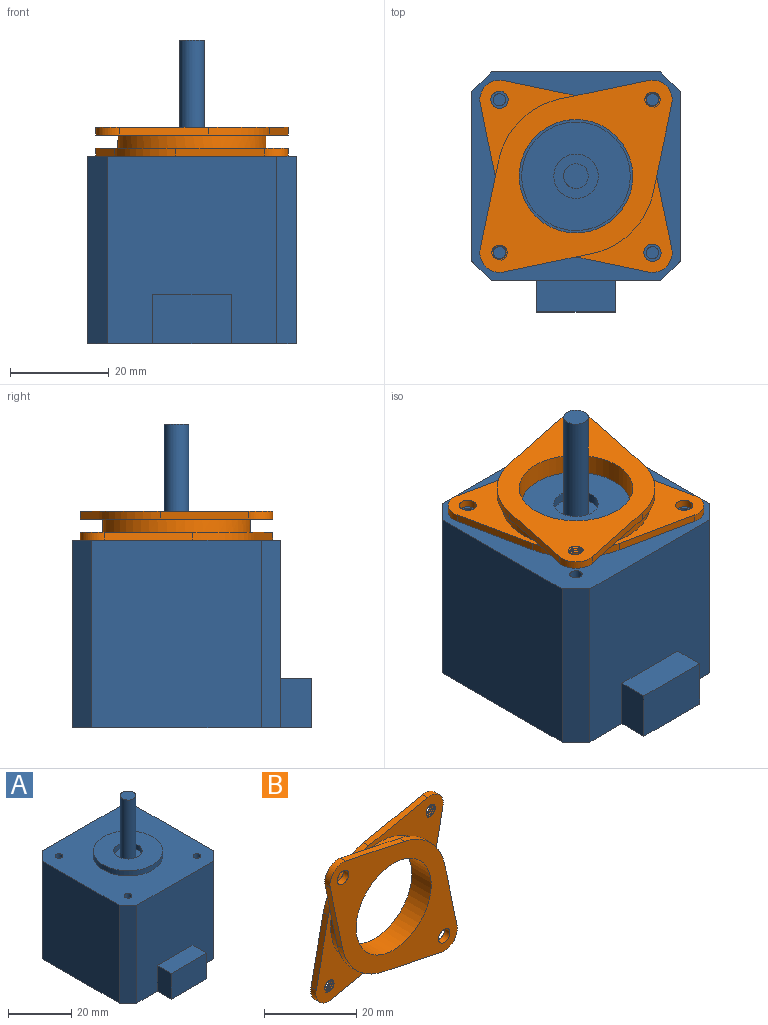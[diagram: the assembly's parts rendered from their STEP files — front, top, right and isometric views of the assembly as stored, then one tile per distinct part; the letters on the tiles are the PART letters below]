
ASSEMBLY  parts=2 mates=1
PART A: 28 faces, bbox 42.3x48.6x61.5 mm
  f0: plane 38x34.3mm, normal (0,-1,0), area 1143.4mm2, adj f4,f5,f20,f21,f22,f26,f27
  f1: plane 38x34.3mm, normal (1,0,0), area 1303.4mm2, adj f4,f5,f25,f26
  f2: plane 38x34.3mm, normal (0,1,0), area 1303.4mm2, adj f4,f5,f24,f25
  f3: plane 38x34.3mm, normal (-1,0,0), area 1303.4mm2, adj f4,f5,f24,f27
  f4: plane 48.6x42.3mm, normal (0,0,-1), area 1858.1mm2, adj f0,f1,f2,f3,f20,f22,f23,f24
  f5: plane 42.3x42.3mm, normal (0,0,1), area 1357.5mm2, adj f0,f1,f2,f3,f6,f8,f10,f12
  f6: cylinder r=1.25mm len=5mm, axis (0,0,1), area 39.3mm2, adj f5,f7
  f7: plane 2.5x2.5mm, normal (0,0,1), area 4.9mm2, adj f6
  f8: cylinder r=1.25mm len=5mm, axis (0,0,1), area 39.3mm2, adj f5,f9
  f9: plane 2.5x2.5mm, normal (0,0,1), area 4.9mm2, adj f8
  f10: cylinder r=1.25mm len=5mm, axis (0,0,1), area 39.3mm2, adj f5,f11
  f11: plane 2.5x2.5mm, normal (0,0,1), area 4.9mm2, adj f10
  f12: cylinder r=1.25mm len=5mm, axis (0,0,1), area 39.3mm2, adj f5,f13
  f13: plane 2.5x2.5mm, normal (0,0,1), area 4.9mm2, adj f12
  f14: cylinder r=4.5mm len=9mm, axis (0,0,-1), area 56.5mm2, adj f16,f17
  f15: cylinder r=11mm len=22mm, axis (0,0,-1), area 138.2mm2, adj f5,f16
  f16: plane 22x22mm, normal (0,0,1), area 316.5mm2, adj f14,f15
  f17: plane 9x9mm, normal (0,0,1), area 44mm2, adj f14,f19
  f18: plane 5x5mm, normal (0,0,1), area 19.6mm2, adj f19
  f19: cylinder r=2.5mm len=23.5mm, axis (0,0,-1), area 369.1mm2, adj f17,f18
  f20: plane 10x6.3mm, normal (1,0,0), area 63mm2, adj f0,f4,f21,f23
  f21: plane 16x6.3mm, normal (0,0,1), area 100.8mm2, adj f0,f20,f22,f23
  f22: plane 10x6.3mm, normal (-1,0,0), area 63mm2, adj f0,f4,f21,f23
  f23: plane 16x10mm, normal (0,-1,0), area 160mm2, adj f4,f20,f21,f22
  f24: plane 38x4mm, normal (-0.71,0.71,0), area 215mm2, adj f2,f3,f4,f5
  f25: plane 38x4mm, normal (0.71,0.71,0), area 215mm2, adj f1,f2,f4,f5
  f26: plane 38x4mm, normal (0.71,-0.71,0), area 215mm2, adj f0,f1,f4,f5
  f27: plane 38x4mm, normal (-0.71,-0.71,0), area 215mm2, adj f0,f3,f4,f5
PART B: 32 faces, bbox 39.1x6.2x39.1 mm
  f0: cylinder r=1.75mm len=3.5mm, axis (0,1,0), area 17.6mm2, adj f10,f11
  f1: cylinder r=1.75mm len=3.5mm, axis (0,1,0), area 17.6mm2, adj f10,f11
  f2: plane 17.96x3.75mm, normal (-0.2,0,-0.98), area 29.3mm2, adj f3,f9,f10,f11
  f3: cylinder r=4mm len=4.82mm, axis (0,1,0), area 12.7mm2, adj f2,f4,f10,f11
  f4: plane 17.96x3.75mm, normal (0.98,0,0.2), area 29.3mm2, adj f3,f5,f10,f11
  f5: cylinder r=16mm len=12.39mm, axis (0,1,0), area 29.7mm2, adj f4,f6,f10,f11
  f6: plane 17.96x3.75mm, normal (0.2,0,0.98), area 29.3mm2, adj f5,f7,f10,f11
  f7: cylinder r=4mm len=4.82mm, axis (0,1,0), area 12.7mm2, adj f6,f8,f10,f11
  f8: plane 17.96x3.75mm, normal (-0.98,0,-0.2), area 29.3mm2, adj f7,f9,f10,f11
  f9: cylinder r=16mm len=12.39mm, axis (0,1,0), area 29.7mm2, adj f2,f8,f10,f11
  f10: plane 39x39mm, normal (0,1,0), area 336mm2, adj f0,f1,f2,f3,f4,f5,f6,f7
  f11: plane 39x39mm, normal (0,-1,0), area 627.4mm2, adj f0,f1,f2,f3,f4,f5,f6,f7
  f12: plane 39.14x39.14mm, normal (0,1,0), area 633.9mm2, adj f14,f15,f16,f17,f18,f19,f20,f21
  f13: cylinder r=15mm len=30mm, axis (0,1,0), area 254.5mm2, adj f10,f31
  f14: cylinder r=11.5mm len=23mm, axis (0,-1,0), area 426.3mm2, adj f11,f12
  f15: cylinder r=1.54mm len=3.09mm, axis (0,1,0), area 3.6mm2, adj f12,f16,f17,f31
  f16: bspline ~3.58x3.57mm, area 9.1mm2, adj f12,f15,f22,f31
  f17: bspline ~3.59x3.58mm, area 9.1mm2, adj f12,f15,f22,f31
  f18: cylinder r=1.54mm len=3.09mm, axis (0,1,0), area 3.6mm2, adj f12,f19,f20,f31
  f19: bspline ~3.58x3.57mm, area 9.1mm2, adj f12,f18,f21,f31
  f20: bspline ~3.59x3.58mm, area 9.1mm2, adj f12,f18,f21,f31
  f21: cylinder r=1.26mm len=2.53mm, axis (0,1,0), area 1.5mm2, adj f12,f19,f20,f31
  f22: cylinder r=1.26mm len=2.53mm, axis (0,1,0), area 1.5mm2, adj f12,f16,f17,f31
  f23: plane 17.96x3.75mm, normal (0.2,0,-0.98), area 29.3mm2, adj f12,f24,f30,f31
  f24: cylinder r=16mm len=12.39mm, axis (0,1,0), area 29.7mm2, adj f12,f23,f25,f31
  f25: plane 17.96x3.75mm, normal (0.98,0,-0.2), area 29.3mm2, adj f12,f24,f26,f31
  f26: cylinder r=4mm len=4.82mm, axis (0,1,0), area 12.7mm2, adj f12,f25,f27,f31
  f27: plane 17.96x3.75mm, normal (-0.2,0,0.98), area 29.3mm2, adj f12,f26,f28,f31
  f28: cylinder r=16mm len=12.39mm, axis (0,1,0), area 29.7mm2, adj f12,f27,f29,f31
  f29: plane 17.96x3.75mm, normal (-0.98,0,0.2), area 29.3mm2, adj f12,f28,f30,f31
  f30: cylinder r=4mm len=4.82mm, axis (0,1,0), area 12.7mm2, adj f12,f23,f29,f31
  f31: plane 39.14x39.14mm, normal (0,-1,0), area 342.6mm2, adj f13,f15,f16,f17,f18,f19,f20,f21
PLACE A at identity fixed
PLACE B rot(axis=(0.58,0.58,0.58),120deg) t=(0,0,0)mm
MATE fastened A.f15 <-> B.f5  axis (0,0,1) through (0,0,0)mm
